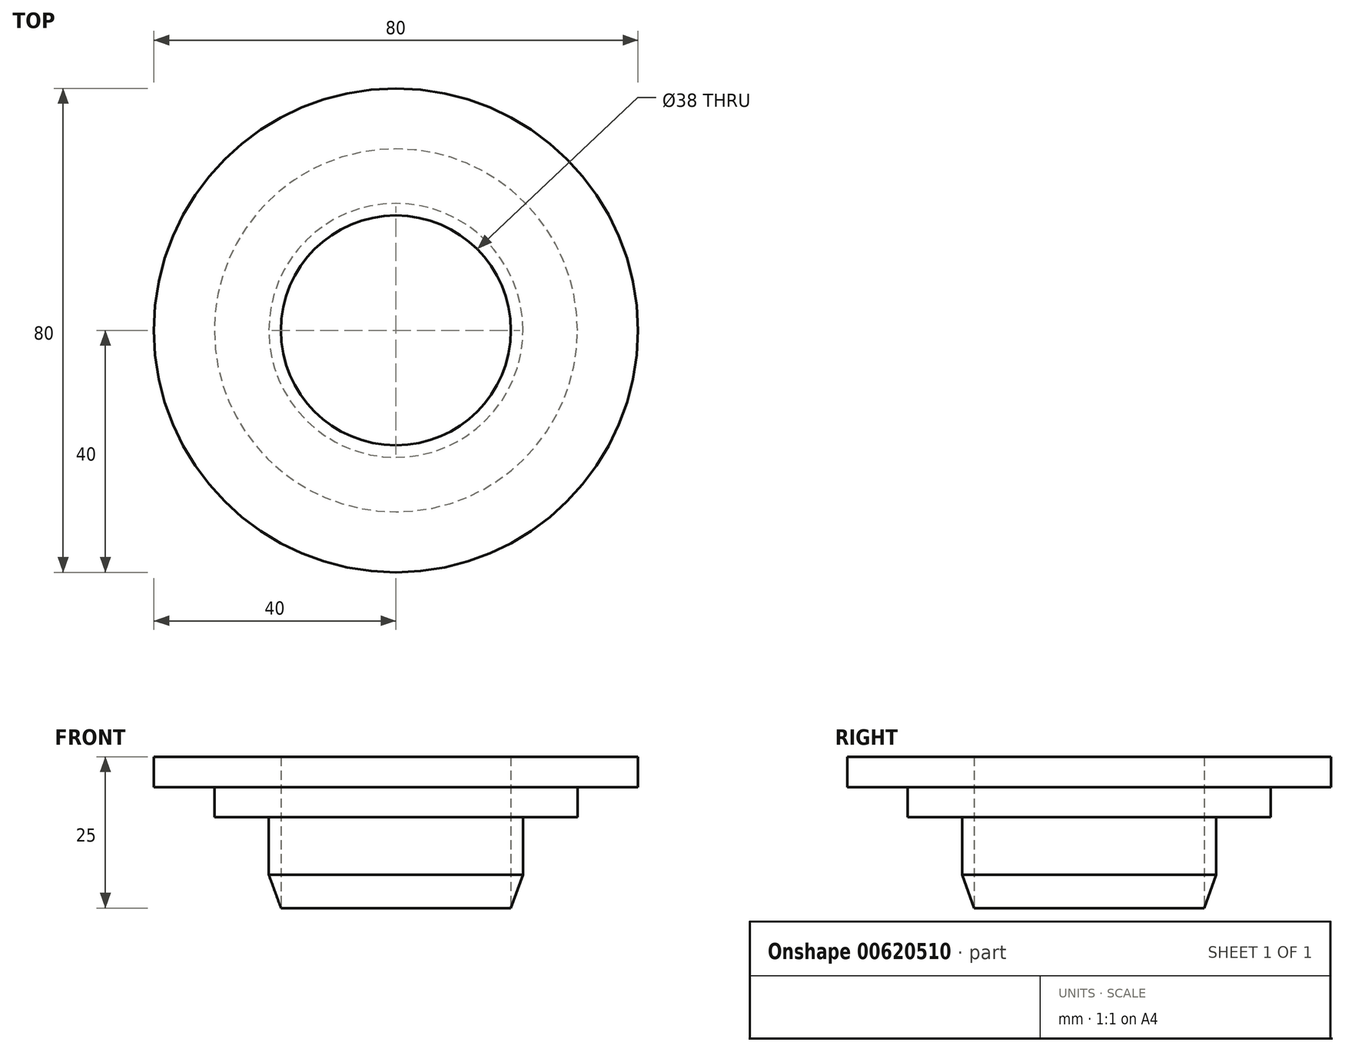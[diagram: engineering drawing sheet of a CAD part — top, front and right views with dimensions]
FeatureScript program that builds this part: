
annotation { "Feature Type Name" : "Feature", "Feature Type Description" : "" }
export const myFeature = defineFeature(function(context is Context, id is Id, definition is map)
    precondition{}
    {
        {
            var Q0;
            Q0=qCreatedBy(makeId("Front.planeOp"),FACE);
            var sketch = newSketch(context, id + "F0", { "sketchPlane" : qUnion([Q0])});
            skLineSegment(sketch, "E0", {"start": v(-19, 0) * mm, "end": v(-19, 25) * mm});
            skLineSegment(sketch, "E1", {"start": v(-19, 25) * mm, "end": v(-40, 25) * mm});
            skLineSegment(sketch, "E2", {"start": v(-40, 25) * mm, "end": v(-40, 20) * mm});
            skLineSegment(sketch, "E3", {"start": v(-21, 5.5) * mm, "end": v(-19, 0) * mm});
            skLineSegment(sketch, "E4", {"start": v(-40, 20) * mm, "end": v(-30, 20) * mm});
            skLineSegment(sketch, "E5", {"start": v(-30, 20) * mm, "end": v(-30, 15) * mm});
            skLineSegment(sketch, "E6", {"start": v(-30, 15) * mm, "end": v(-21, 15) * mm});
            skLineSegment(sketch, "E7", {"start": v(-21, 15) * mm, "end": v(-21, 5.5) * mm});
            skLineSegment(sketch, "E8", {"start": v(0, 0) * mm, "end": v(0, 47.42) * mm, "construction": true});
            skSolve(sketch);
        }
        {
            var Q0;
            Q0=makeQuery(id+"F0.imprint","IMPRINT",FACE,{"disambiguationData":[TD([[makeQuery(id+"F0.imprint","IMPRINT",EDGE,{"derivedFrom":sQuery(id+"F0.wireOp",EDGE,"E0")}),1.0]])]});
            var Q1;
            Q1=sQuery(id+"F0.wireOp",EDGE,"E8");
            revolve(context, id + "F1", {"entities" : qUnion([Q0]), "axis" : qUnion([Q1]), "revolveType" : RevolveType.FULL});
        }
    });
